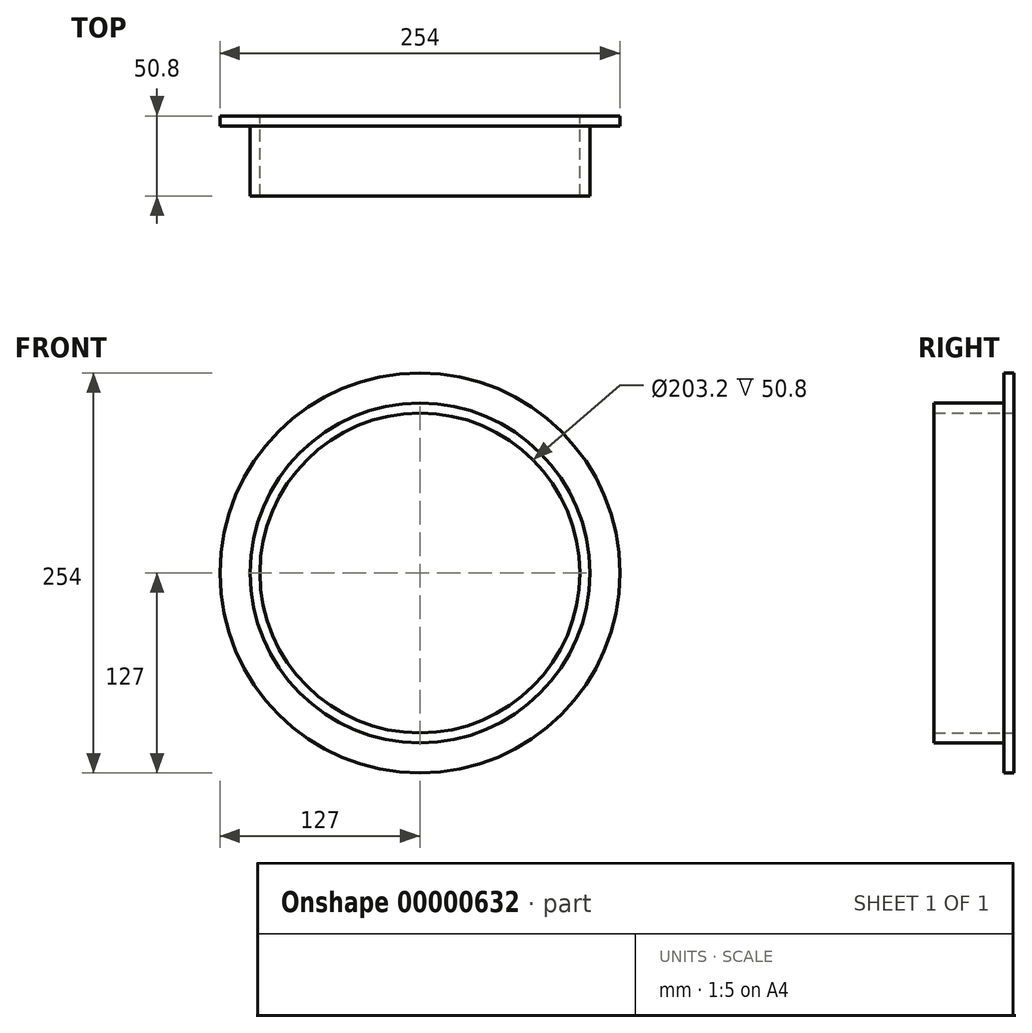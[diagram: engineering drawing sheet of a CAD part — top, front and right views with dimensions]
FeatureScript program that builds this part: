
annotation { "Feature Type Name" : "Feature", "Feature Type Description" : "" }
export const myFeature = defineFeature(function(context is Context, id is Id, definition is map)
    precondition{}
    {
        {
            var Q0;
            Q0=qCreatedBy(makeId("Front.planeOp"),FACE);
            var sketch = newSketch(context, id + "F0", { "sketchPlane" : qUnion([Q0])});
            skCircle(sketch, "E0", {"center": v(0, 0) * mm, "radius": 101.6 * mm});
            skCircle(sketch, "E1", {"center": v(0, 0) * mm, "radius": 127 * mm});
            skCircle(sketch, "E2", {"center": v(0, 0) * mm, "radius": 107.95 * mm});
            skSolve(sketch);
        }
        {
            var Q0;
            Q0=makeQuery(id+"F0.imprint","IMPRINT",FACE,{"disambiguationData":[TD([[makeQuery(id+"F0.imprint","IMPRINT",EDGE,{"derivedFrom":sQuery(id+"F0.wireOp",EDGE,"E0")}),-1.0]])]});
            extrude(context, id + "F1", {"entities" : qUnion([Q0]), "depth" : 50.8 * mm});
        }
        {
            var Q0;
            Q0=makeQuery(id+"F0.imprint","IMPRINT",FACE,{"disambiguationData":[TD([[makeQuery(id+"F0.imprint","IMPRINT",EDGE,{"derivedFrom":sQuery(id+"F0.wireOp",EDGE,"E1")}),1.0]])]});
            extrude(context, id + "F2", {"entities" : qUnion([Q0]), "operationType" : NewBodyOperationType.ADD, "depth" : 6.35 * mm});
        }
    });
